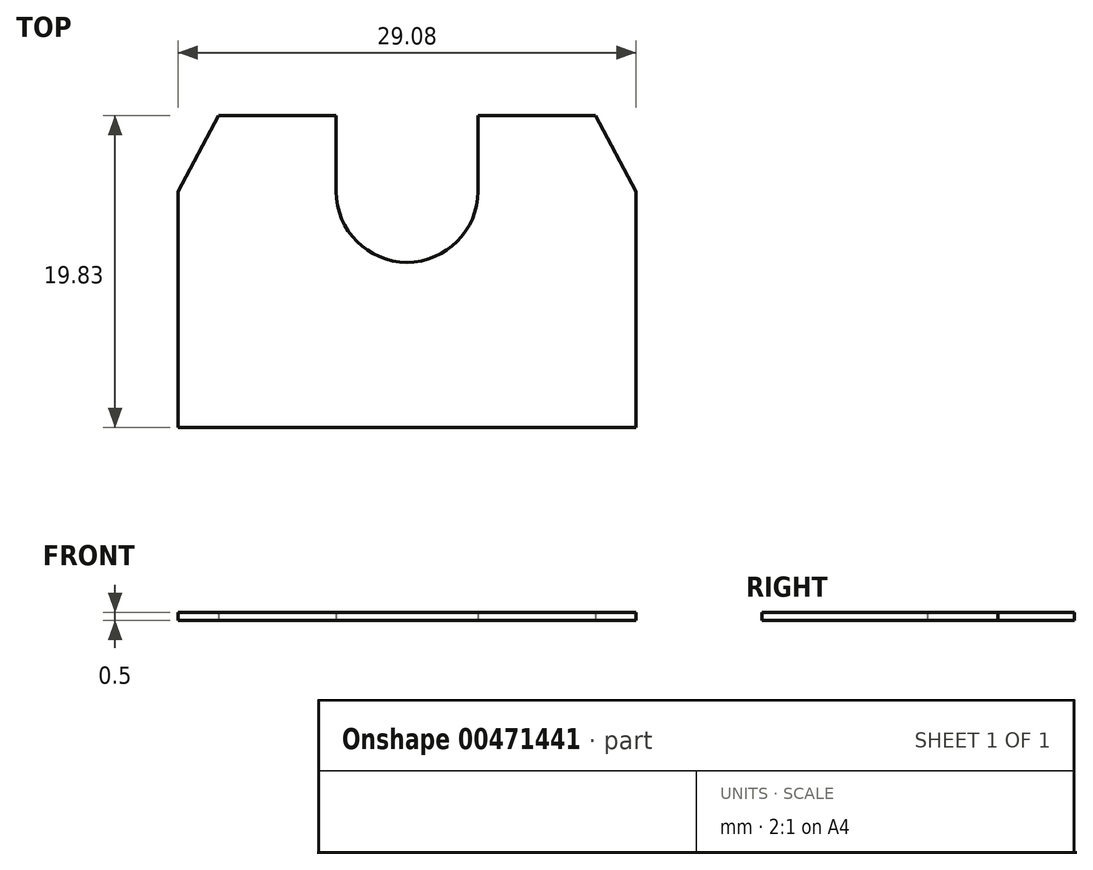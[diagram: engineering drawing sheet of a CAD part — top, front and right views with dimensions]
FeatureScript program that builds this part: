
annotation { "Feature Type Name" : "Feature", "Feature Type Description" : "" }
export const myFeature = defineFeature(function(context is Context, id is Id, definition is map)
    precondition{}
    {
        {
            var Q0;
            Q0=qCreatedBy(makeId("Top.planeOp"),FACE);
            var sketch = newSketch(context, id + "F0", { "sketchPlane" : qUnion([Q0])});
            skArc(sketch, "E0", {"start": v(-4.5, 0) * mm, "mid": v(0, -4.5) * mm, "end": v(4.5, 0) * mm});
            skLineSegment(sketch, "E1", {"start": v(-4.5, 0) * mm, "end": v(-4.5, 4.83) * mm});
            skLineSegment(sketch, "E2", {"start": v(-4.5, 4.83) * mm, "end": v(-11.98, 4.83) * mm});
            skLineSegment(sketch, "E3", {"start": v(-11.98, 4.83) * mm, "end": v(-14.54, 0) * mm});
            skLineSegment(sketch, "E4", {"start": v(-14.54, 0) * mm, "end": v(-14.54, -15) * mm});
            skLineSegment(sketch, "E5", {"start": v(-14.54, -15) * mm, "end": v(0, -15) * mm});
            skLineSegment(sketch, "E6.MirrorCS", {"start": v(4.5, 0) * mm, "end": v(4.5, 4.83) * mm});
            skLineSegment(sketch, "E7.MirrorCS", {"start": v(4.5, 4.83) * mm, "end": v(11.98, 4.83) * mm});
            skLineSegment(sketch, "E8.MirrorCS", {"start": v(11.98, 4.83) * mm, "end": v(14.54, 0) * mm});
            skLineSegment(sketch, "E9.MirrorCS", {"start": v(14.54, 0) * mm, "end": v(14.54, -15) * mm});
            skLineSegment(sketch, "E10.MirrorCS", {"start": v(14.54, -15) * mm, "end": v(0, -15) * mm});
            skSolve(sketch);
        }
        {
            var Q0;
            Q0=makeQuery(id+"F0.imprint","IMPRINT",FACE,{"disambiguationData":[TD([[makeQuery(id+"F0.imprint","IMPRINT",EDGE,{"derivedFrom":sQuery(id+"F0.wireOp",EDGE,"E0")}),-1.0]])]});
            extrude(context, id + "F1", {"entities" : qUnion([Q0]), "depth" : .5 * mm});
        }
    });
